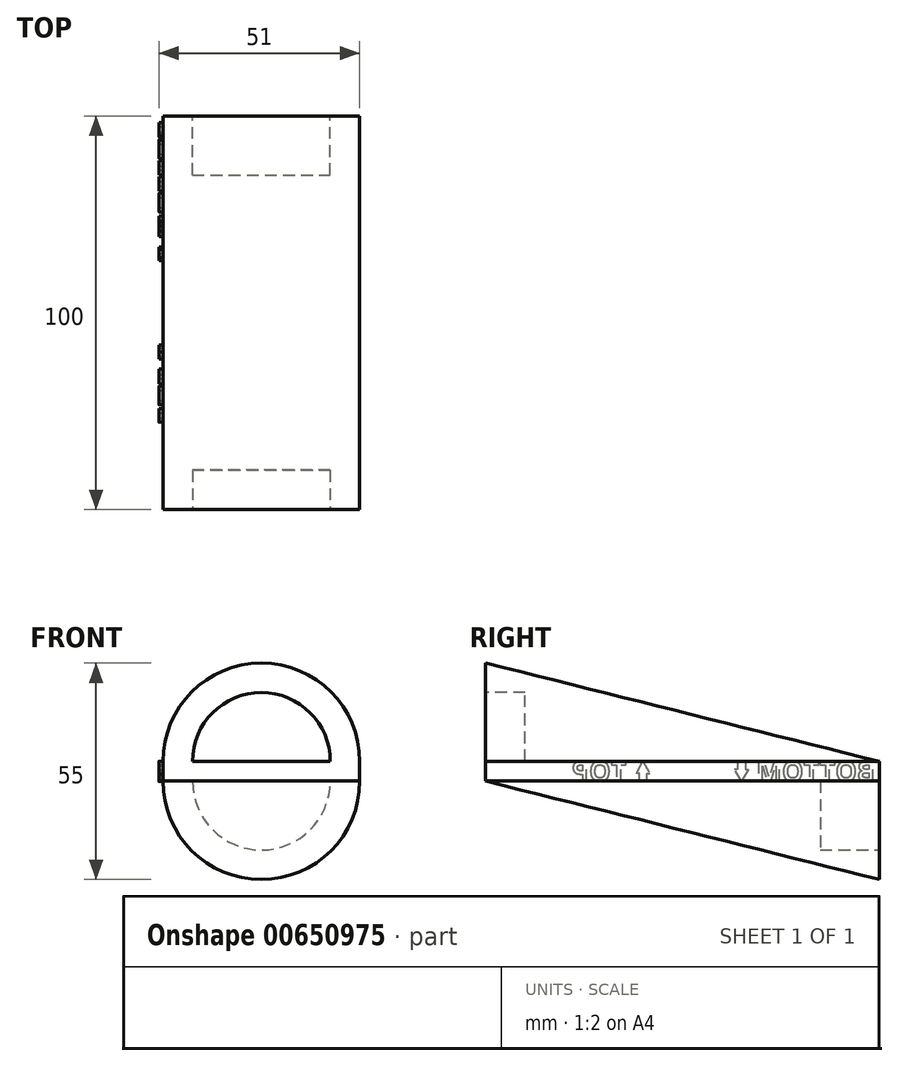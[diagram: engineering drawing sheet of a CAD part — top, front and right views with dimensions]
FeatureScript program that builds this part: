
annotation { "Feature Type Name" : "Feature", "Feature Type Description" : "" }
export const myFeature = defineFeature(function(context is Context, id is Id, definition is map)
    precondition{}
    {
        {
            var Q0;
            Q0=qCreatedBy(makeId("Front.planeOp"),FACE);
            var sketch = newSketch(context, id + "F0", { "sketchPlane" : qUnion([Q0])});
            skLineSegment(sketch, "E0.top", {"start": v(0, 5) * mm, "end": v(50, 5) * mm});
            skLineSegment(sketch, "E0.left", {"start": v(0, 0) * mm, "end": v(0, 5) * mm});
            skLineSegment(sketch, "E0.right", {"start": v(50, 0) * mm, "end": v(50, 5) * mm});
            skArc(sketch, "E1", {"start": v(0, 0) * mm, "mid": v(25, -25) * mm, "end": v(50, 0) * mm});
            skSolve(sketch);
        }
        {
            var Q0;
            Q0=qCreatedBy(makeId("Front.planeOp"),FACE);
            cPlane(context, id + "F1", {"entities" : qUnion([Q0]), "cplaneType" : CPlaneType.OFFSET, "offset" : 100 * mm, "width" : 150 * mm, "height" : 150 * mm});
        }
        {
            var Q0;
            Q0=qCreatedBy(id+"F1.planeOp",FACE);
            var sketch = newSketch(context, id + "F2", { "sketchPlane" : qUnion([Q0])});
            skLineSegment(sketch, "E2.bottom", {"start": v(0, 0) * mm, "end": v(50, 0) * mm});
            skLineSegment(sketch, "E2.left", {"start": v(0, 0) * mm, "end": v(0, 5) * mm});
            skLineSegment(sketch, "E2.right", {"start": v(50, 0) * mm, "end": v(50, 5) * mm});
            skArc(sketch, "E3", {"start": v(50, 5) * mm, "mid": v(25, 30) * mm, "end": v(0, 5) * mm});
            skSolve(sketch);
        }
        {
            var Q0;
            Q0=makeQuery(id+"F2.imprint","IMPRINT",FACE,{"disambiguationData":[TD([[makeQuery(id+"F2.imprint","IMPRINT",EDGE,{"derivedFrom":sQuery(id+"F2.wireOp",EDGE,"E2.bottom")}),1.0]])]});
            var Q1;
            Q1=makeQuery(id+"F0.imprint","IMPRINT",FACE,{"disambiguationData":[TD([[makeQuery(id+"F0.imprint","IMPRINT",EDGE,{"derivedFrom":sQuery(id+"F0.wireOp",EDGE,"E0.top")}),-1.0]])]});
            loft(context, id + "F3", {"sheetProfilesArray" : [{ "sheetProfileEntities" : qUnion([Q0]) }, { "sheetProfileEntities" : qUnion([Q1]) }]});
        }
        {
            var Q0;
            Q0=qCreatedBy(id+"F1.planeOp",FACE);
            var sketch = newSketch(context, id + "F4", { "sketchPlane" : qUnion([Q0])});
            skLineSegment(sketch, "E4", {"start": v(7.5, 5) * mm, "end": v(42.5, 5) * mm});
            skArc(sketch, "E5", {"start": v(42.5, 5) * mm, "mid": v(25, 22.5) * mm, "end": v(7.5, 5) * mm});
            skSolve(sketch);
        }
        {
            var Q0;
            Q0=qCreatedBy(makeId("Front.planeOp"),FACE);
            var sketch = newSketch(context, id + "F5", { "sketchPlane" : qUnion([Q0])});
            skLineSegment(sketch, "E6", {"start": v(7.5, 0) * mm, "end": v(42.5, 0) * mm});
            skArc(sketch, "E7", {"start": v(7.5, 0) * mm, "mid": v(25, -17.5) * mm, "end": v(42.5, 0) * mm});
            skSolve(sketch);
        }
        {
            var Q0;
            Q0 = qSketchRegion(id + "F5", true);
            extrude(context, id + "F6", {"entities" : qUnion([Q0]), "operationType" : NewBodyOperationType.REMOVE, "depth" : 15 * mm, "offsetDistance" : 25 * mm});
        }
        {
            var Q0;
            Q0 = qSketchRegion(id + "F4", true);
            extrude(context, id + "F7", {"entities" : qUnion([Q0]), "operationType" : NewBodyOperationType.REMOVE, "oppositeDirection" : true, "depth" : 10 * mm, "offsetDistance" : 25 * mm});
        }
        {
            var Q0;
            Q0=qCreatedBy(makeId("Right.planeOp"),FACE);
            var sketch = newSketch(context, id + "F8", { "sketchPlane" : qUnion([Q0])});
            skLineSegment(sketch, "E8", {"start": v(-35.75, 0) * mm, "end": v(-35.75, 1.97) * mm});
            skLineSegment(sketch, "E9", {"start": v(-35.75, 0) * mm, "end": v(-37.75, 0) * mm});
            skLineSegment(sketch, "E10", {"start": v(-37.75, 0) * mm, "end": v(-37.75, 1.97) * mm});
            skLineSegment(sketch, "E11", {"start": v(-37.75, 1.97) * mm, "end": v(-38.5, 1.97) * mm});
            skLineSegment(sketch, "E12", {"start": v(-35.75, 1.97) * mm, "end": v(-35, 1.97) * mm});
            skLineSegment(sketch, "E13", {"start": v(-35, 1.97) * mm, "end": v(-36.75, 5) * mm});
            skLineSegment(sketch, "E14", {"start": v(-36.75, 5) * mm, "end": v(-38.5, 1.97) * mm});
            skLineSegment(sketch, "E15", {"start": v(-62.75, 5) * mm, "end": v(-62.75, 3.03) * mm});
            skLineSegment(sketch, "E16", {"start": v(-62.75, 5) * mm, "end": v(-60.75, 5) * mm});
            skLineSegment(sketch, "E17", {"start": v(-60.75, 5) * mm, "end": v(-60.75, 3.03) * mm});
            skLineSegment(sketch, "E18", {"start": v(-60.75, 3.03) * mm, "end": v(-60, 3.03) * mm});
            skLineSegment(sketch, "E19", {"start": v(-62.75, 3.03) * mm, "end": v(-63.5, 3.03) * mm});
            skLineSegment(sketch, "E20", {"start": v(-63.5, 3.03) * mm, "end": v(-61.75, 0) * mm});
            skLineSegment(sketch, "E21", {"start": v(-61.75, 0) * mm, "end": v(-60, 3.03) * mm});
            skSolve(sketch);
        }
        {
            var Q0;
            {var subQ0=sQuery(id+"F2.wireOp",EDGE,"E3");var subQ2=sQuery(id+"F2.wireOp",EDGE,"E2.left");var subQ4=sQuery(id+"F0.wireOp",EDGE,"E0.left");var subQ5=sQuery(id+"F0.wireOp",EDGE,"E0.top");var subQ6=sQuery(id+"F2.wireOp",EDGE,"E2.bottom");var subQ7=sQuery(id+"F0.wireOp",EDGE,"E1");var subQ8=makeQuery(id+"F3.opLoft","SWEPT_FACE",FACE,{"disambiguationData":[OSD([subQ5,subQ4,subQ7,subQ6,subQ2,subQ0])]});Q0=makeQuery(id+"FKW33Yl0KWiDohp_1.boolean.opBoolean","SPLIT",FACE,{"disambiguationData":[TD([makeQuery(id+"FKW33Yl0KWiDohp_1.opExtrude","SWEPT_FACE",FACE,{"disambiguationData":[OSD([sQuery(id+"F8.wireOp",EDGE,"E10")])]})])],"derivedFrom":subQ8});}
            var sketch = newSketch(context, id + "F9", { "sketchPlane" : qUnion([Q0])});
            skLineSegment(sketch, "E22", {"start": v(61, 0) * mm, "end": v(61, 1.97) * mm});
            skLineSegment(sketch, "E23", {"start": v(61, 0) * mm, "end": v(59, 0) * mm});
            skLineSegment(sketch, "E24", {"start": v(59, 0) * mm, "end": v(59, 1.97) * mm});
            skLineSegment(sketch, "E25", {"start": v(59, 1.97) * mm, "end": v(58.25, 1.97) * mm});
            skLineSegment(sketch, "E26", {"start": v(61, 1.97) * mm, "end": v(61.75, 1.97) * mm});
            skLineSegment(sketch, "E27", {"start": v(61.75, 1.97) * mm, "end": v(60, 5) * mm});
            skLineSegment(sketch, "E28", {"start": v(60, 5) * mm, "end": v(58.25, 1.97) * mm});
            skLineSegment(sketch, "E29", {"start": v(34, 5) * mm, "end": v(34, 3.03) * mm});
            skLineSegment(sketch, "E30", {"start": v(34, 5) * mm, "end": v(36, 5) * mm});
            skLineSegment(sketch, "E31", {"start": v(36, 5) * mm, "end": v(36, 3.03) * mm});
            skLineSegment(sketch, "E32", {"start": v(36, 3.03) * mm, "end": v(36.75, 3.03) * mm});
            skLineSegment(sketch, "E33", {"start": v(34, 3.03) * mm, "end": v(33.25, 3.03) * mm});
            skLineSegment(sketch, "E34", {"start": v(33.25, 3.03) * mm, "end": v(35, 0) * mm});
            skLineSegment(sketch, "E35", {"start": v(35, 0) * mm, "end": v(36.75, 3.03) * mm});
            skText(sketch, "E36", { "text": "BOTTOM", "fontName": "OpenSans-Bold.ttf"});
            skText(sketch, "E37", { "text": "TOP", "fontName": "OpenSans-Bold.ttf"});
            const initialGuessF9  = {"E36": [0.001, -2e-05, 1, 0, 0.005], "E37": [0.0642, 0, 1, 0, 0.005]};
            skSetInitialGuess(sketch, initialGuessF9);
            skSolve(sketch);
        }
        {
            var Q0;
            Q0 = qSketchRegion(id + "F9", true);
            extrude(context, id + "F10", {"entities" : qUnion([Q0]), "operationType" : NewBodyOperationType.ADD, "depth" : 1 * mm, "offsetDistance" : 25 * mm});
        }
    });
